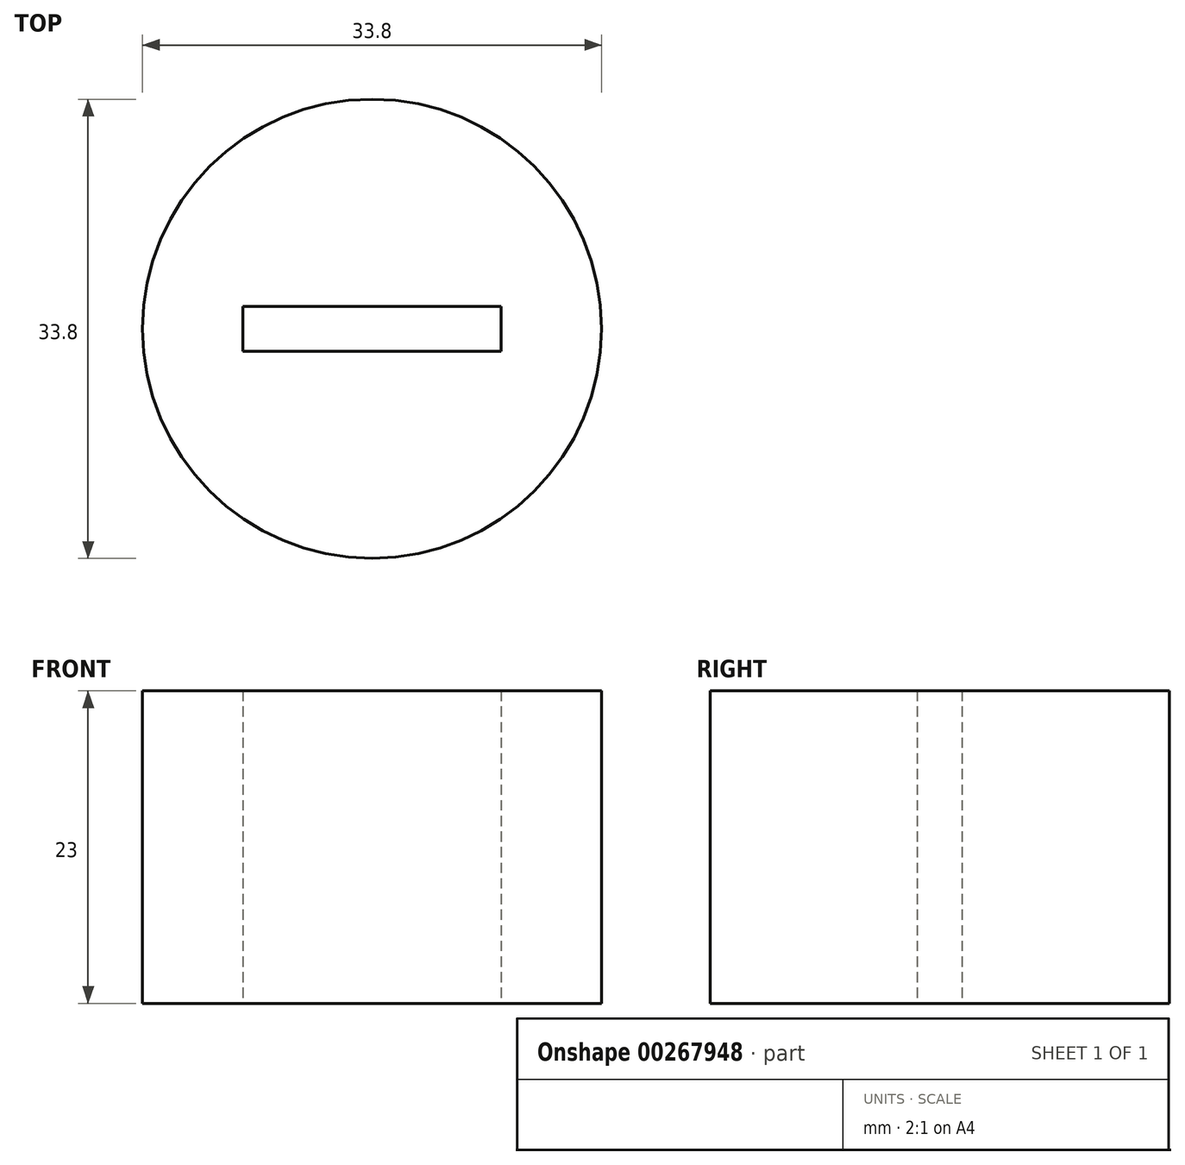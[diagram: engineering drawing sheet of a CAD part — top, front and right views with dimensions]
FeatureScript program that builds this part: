
annotation { "Feature Type Name" : "Feature", "Feature Type Description" : "" }
export const myFeature = defineFeature(function(context is Context, id is Id, definition is map)
    precondition{}
    {
        {
            var Q0;
            Q0=qCreatedBy(makeId("Top.planeOp"),FACE);
            var sketch = newSketch(context, id + "F0", { "sketchPlane" : qUnion([Q0])});
            skLineSegment(sketch, "E0", {"start": v(-44.17, 0) * mm, "end": v(45.06, 0) * mm, "construction": true});
            skLineSegment(sketch, "E1", {"start": v(0, 44.35) * mm, "end": v(0, -35.7) * mm, "construction": true});
            skCircle(sketch, "E2", {"center": v(0, 0) * mm, "radius": 16.9 * mm});
            skLineSegment(sketch, "E3", {"start": v(-9.5, 0) * mm, "end": v(-9.5, 1.65) * mm});
            skLineSegment(sketch, "E4", {"start": v(0, 1.65) * mm, "end": v(-9.5, 1.65) * mm});
            skLineSegment(sketch, "E5.MirrorCS", {"start": v(0, -1.65) * mm, "end": v(-9.5, -1.65) * mm});
            skLineSegment(sketch, "E6.MirrorCS", {"start": v(-9.5, 0) * mm, "end": v(-9.5, -1.65) * mm});
            skLineSegment(sketch, "E7.MirrorCS", {"start": v(9.5, 0) * mm, "end": v(9.5, 1.65) * mm});
            skLineSegment(sketch, "E8.MirrorCS", {"start": v(9.5, 0) * mm, "end": v(9.5, -1.65) * mm});
            skLineSegment(sketch, "E9.MirrorCS", {"start": v(0, 1.65) * mm, "end": v(9.5, 1.65) * mm});
            skLineSegment(sketch, "E10.MirrorCS", {"start": v(0, -1.65) * mm, "end": v(9.5, -1.65) * mm});
            skSolve(sketch);
        }
        {
            var Q0;
            Q0=makeQuery(id+"F0.imprint","IMPRINT",FACE,{"disambiguationData":[TD([[makeQuery(id+"F0.imprint","IMPRINT",EDGE,{"derivedFrom":sQuery(id+"F0.wireOp",EDGE,"E2")}),1.0]])]});
            extrude(context, id + "F1", {"entities" : qUnion([Q0]), "depth" : 23 * mm});
        }
    });
